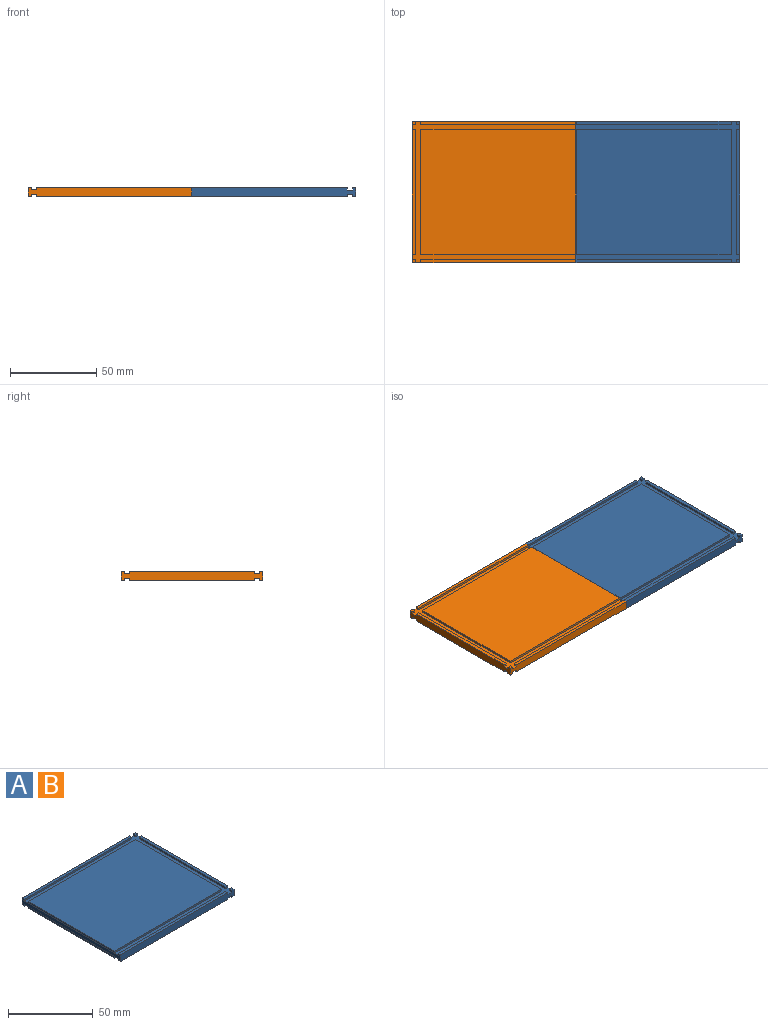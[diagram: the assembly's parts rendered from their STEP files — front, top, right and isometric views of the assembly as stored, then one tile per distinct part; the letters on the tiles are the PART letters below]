
ASSEMBLY  parts=2 mates=1
PART A: 50 faces, bbox 95x82.3x4.9 mm
  f0: plane 95x4.9mm, normal (0,-1,0), area 457.8mm2, adj f1,f2,f5,f7,f8,f11,f20,f21
  f1: plane 82.25x4.9mm, normal (1,0,0), area 387.5mm2, adj f0,f2,f3,f4,f8,f9,f10,f13
  f2: plane 1.91x1.91mm, normal (0,0,-1), area 3.6mm2, adj f0,f1,f39,f40
  f3: plane 72.09x1.91mm, normal (0,0,-1), area 137.3mm2, adj f1,f41,f42,f43
  f4: plane 1.91x1.91mm, normal (0,0,-1), area 3.6mm2, adj f1,f13,f44,f45
  f5: plane 89.92x1.91mm, normal (0,0,-1), area 171.3mm2, adj f0,f7,f37,f38
  f6: plane 89.84x1.91mm, normal (0,0,-1), area 171.1mm2, adj f13,f35,f36,f46
  f7: plane 82.25x4.9mm, normal (-1,0,0), area 207mm2, adj f0,f5,f11,f13,f19,f30,f37,f48
  f8: plane 1.91x1.91mm, normal (0,0,1), area 3.6mm2, adj f0,f1,f21,f22
  f9: plane 72.09x1.91mm, normal (0,0,1), area 137.3mm2, adj f1,f23,f24,f25
  f10: plane 1.91x1.91mm, normal (0,0,1), area 3.6mm2, adj f1,f13,f26,f27
  f11: plane 89.92x1.91mm, normal (0,0,1), area 171.3mm2, adj f0,f7,f19,f20
  f12: plane 89.84x1.91mm, normal (0,0,1), area 171.1mm2, adj f13,f17,f18,f28
  f13: plane 95x4.9mm, normal (0,1,0), area 457.6mm2, adj f1,f4,f6,f7,f10,f12,f18,f27
  f14: plane 72.09x1.27mm, normal (-1,0,0), area 91.6mm2, adj f15,f29,f30,f31
  f15: plane 89.84x1.27mm, normal (0,1,0), area 114.1mm2, adj f14,f16,f30,f31
  f16: plane 72.09x1.27mm, normal (1,0,0), area 91.6mm2, adj f15,f29,f30,f31
  f17: plane 89.84x1.27mm, normal (0,-1,0), area 114.1mm2, adj f12,f18,f28,f30
  f18: plane 1.91x1.27mm, normal (-1,0,0), area 2.4mm2, adj f12,f13,f17,f30
  f19: plane 89.92x1.27mm, normal (0,1,0), area 114.2mm2, adj f7,f11,f20,f30
  f20: plane 1.91x1.27mm, normal (1,0,0), area 2.4mm2, adj f0,f11,f19,f30
  f21: plane 1.91x1.27mm, normal (-1,0,0), area 2.4mm2, adj f0,f8,f22,f30
  f22: plane 1.91x1.27mm, normal (0,1,0), area 2.4mm2, adj f1,f8,f21,f30
  f23: plane 1.91x1.27mm, normal (0,-1,0), area 2.4mm2, adj f1,f9,f24,f30
  f24: plane 72.09x1.27mm, normal (-1,0,0), area 91.6mm2, adj f9,f23,f25,f30
  f25: plane 1.91x1.27mm, normal (0,1,0), area 2.4mm2, adj f1,f9,f24,f30
  f26: plane 1.91x1.27mm, normal (0,-1,0), area 2.4mm2, adj f1,f10,f27,f30
  f27: plane 1.91x1.27mm, normal (-1,0,0), area 2.4mm2, adj f10,f13,f26,f30
  f28: plane 1.91x1.27mm, normal (1,0,0), area 2.4mm2, adj f12,f13,f17,f30
  f29: plane 89.84x1.27mm, normal (0,-1,0), area 114.1mm2, adj f14,f16,f30,f31
  f30: plane 95x82.25mm, normal (0,0,1), area 850.2mm2, adj f0,f1,f7,f13,f14,f15,f16,f17
  f31: plane 89.84x72.09mm, normal (0,0,1), area 6476.6mm2, adj f14,f15,f16,f29
  f32: plane 72.09x1.17mm, normal (-1,0,0), area 84.3mm2, adj f33,f47,f48,f49
  f33: plane 89.84x1.17mm, normal (0,1,0), area 105.1mm2, adj f32,f34,f48,f49
  f34: plane 72.09x1.17mm, normal (1,0,0), area 84.3mm2, adj f33,f47,f48,f49
  f35: plane 89.84x1.17mm, normal (0,-1,0), area 105.1mm2, adj f6,f36,f46,f48
  f36: plane 1.91x1.17mm, normal (-1,0,0), area 2.2mm2, adj f6,f13,f35,f48
  f37: plane 89.92x1.17mm, normal (0,1,0), area 105.2mm2, adj f5,f7,f38,f48
  f38: plane 1.91x1.17mm, normal (1,0,0), area 2.2mm2, adj f0,f5,f37,f48
  f39: plane 1.91x1.17mm, normal (-1,0,0), area 2.2mm2, adj f0,f2,f40,f48
  f40: plane 1.91x1.17mm, normal (0,1,0), area 2.2mm2, adj f1,f2,f39,f48
  f41: plane 1.91x1.17mm, normal (0,-1,0), area 2.2mm2, adj f1,f3,f42,f48
  f42: plane 72.09x1.17mm, normal (-1,0,0), area 84.3mm2, adj f3,f41,f43,f48
  f43: plane 1.91x1.17mm, normal (0,1,0), area 2.2mm2, adj f1,f3,f42,f48
  f44: plane 1.91x1.17mm, normal (0,-1,0), area 2.2mm2, adj f1,f4,f45,f48
  f45: plane 1.91x1.17mm, normal (-1,0,0), area 2.2mm2, adj f4,f13,f44,f48
  f46: plane 1.91x1.17mm, normal (1,0,0), area 2.2mm2, adj f6,f13,f35,f48
  f47: plane 89.84x1.17mm, normal (0,-1,0), area 105.1mm2, adj f32,f34,f48,f49
  f48: plane 95x82.25mm, normal (0,0,-1), area 850.2mm2, adj f0,f1,f7,f13,f32,f33,f34,f35
  f49: plane 89.84x72.09mm, normal (0,0,-1), area 6476.6mm2, adj f32,f33,f34,f47
PART B: same geometry as A
PLACE A t=(45,-146.28,0.05)mm
PLACE B rot(axis=(0,0,-1),180deg) t=(-45,-146.29,0.1)mm
MATE parallel B.f13 <-> A.f0  axis (0,-1,0) through (0,-187.41,2.5)mm
